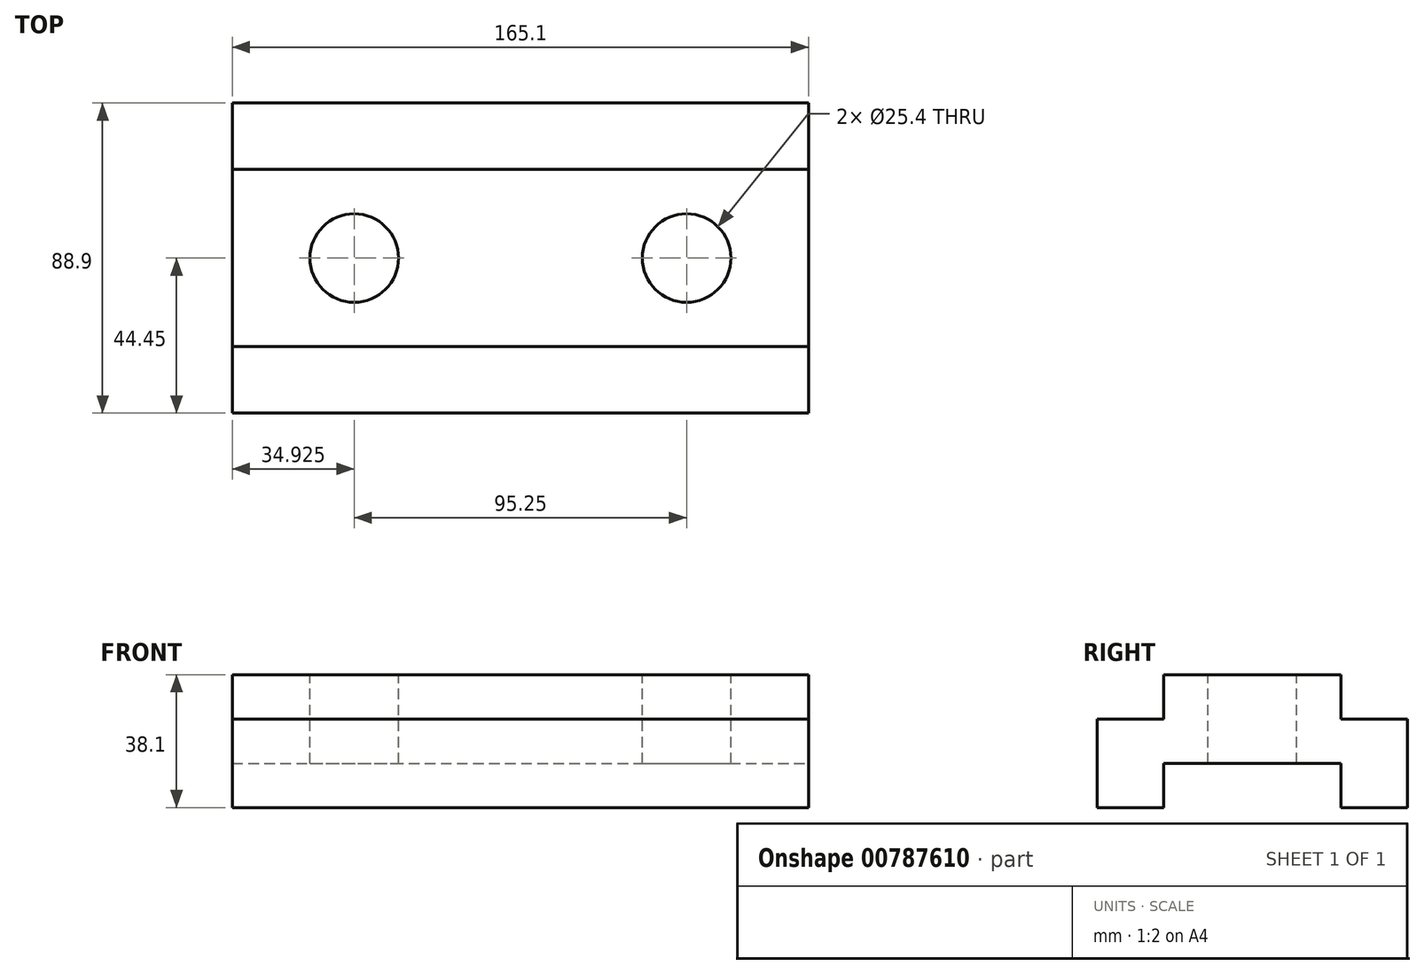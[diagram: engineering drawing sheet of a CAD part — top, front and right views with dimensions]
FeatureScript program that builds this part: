
annotation { "Feature Type Name" : "Feature", "Feature Type Description" : "" }
export const myFeature = defineFeature(function(context is Context, id is Id, definition is map)
    precondition{}
    {
        {
            var Q0;
            Q0=qCreatedBy(makeId("Right.planeOp"),FACE);
            var sketch = newSketch(context, id + "F0", { "sketchPlane" : qUnion([Q0])});
            skLineSegment(sketch, "E0", {"start": v(0, 0) * mm, "end": v(0, 25.4) * mm});
            skLineSegment(sketch, "E1", {"start": v(0, 25.4) * mm, "end": v(19.05, 25.4) * mm});
            skLineSegment(sketch, "E2", {"start": v(19.05, 25.4) * mm, "end": v(19.05, 38.1) * mm});
            skLineSegment(sketch, "E3", {"start": v(19.05, 38.1) * mm, "end": v(69.85, 38.1) * mm});
            skLineSegment(sketch, "E4", {"start": v(69.85, 38.1) * mm, "end": v(69.85, 25.4) * mm});
            skLineSegment(sketch, "E5", {"start": v(69.85, 25.4) * mm, "end": v(88.9, 25.4) * mm});
            skLineSegment(sketch, "E6", {"start": v(88.9, 25.4) * mm, "end": v(88.9, 0) * mm});
            skLineSegment(sketch, "E7", {"start": v(88.9, 0) * mm, "end": v(0, 0) * mm});
            skSolve(sketch);
        }
        {
            var Q0;
            Q0=makeQuery(id+"F0.imprint","IMPRINT",FACE,{"disambiguationData":[TD([[makeQuery(id+"F0.imprint","IMPRINT",EDGE,{"derivedFrom":sQuery(id+"F0.wireOp",EDGE,"E0")}),-1.0]])]});
            extrude(context, id + "F1", {"entities" : qUnion([Q0]), "depth" : 165.1 * mm, "offsetDistance" : 25.4 * mm});
        }
        {
            var Q0;
            Q0=makeQuery(id+"F1.opExtrude","CAP_FACE",FACE,{"disambiguationData":[OSD([sQuery(id+"F0.wireOp",EDGE,"E0"),sQuery(id+"F0.wireOp",EDGE,"E1"),sQuery(id+"F0.wireOp",EDGE,"E2"),sQuery(id+"F0.wireOp",EDGE,"E3"),sQuery(id+"F0.wireOp",EDGE,"E4"),sQuery(id+"F0.wireOp",EDGE,"E5"),sQuery(id+"F0.wireOp",EDGE,"E6"),sQuery(id+"F0.wireOp",EDGE,"E7")])],"isStart":false});
            var sketch = newSketch(context, id + "F2", { "sketchPlane" : qUnion([Q0])});
            skLineSegment(sketch, "E8", {"start": v(0, 0) * mm, "end": v(19.05, 0) * mm});
            skLineSegment(sketch, "E9", {"start": v(19.05, 0) * mm, "end": v(19.05, 12.7) * mm});
            skLineSegment(sketch, "E10", {"start": v(19.05, 12.7) * mm, "end": v(69.85, 12.7) * mm});
            skLineSegment(sketch, "E11", {"start": v(69.85, 12.7) * mm, "end": v(69.85, 0) * mm});
            skLineSegment(sketch, "E12", {"start": v(69.85, 0) * mm, "end": v(88.9, 0) * mm});
            skSolve(sketch);
        }
        {
            var Q0;
            {var subQ0=sQuery(id+"F2.wireOp",EDGE,"E9");Q0=makeQuery(id+"F2.imprint","IMPRINT",FACE,{"disambiguationData":[TD([[makeQuery(id+"F2.imprint","IMPRINT",EDGE,{"derivedFrom":subQ0}),-1.0]])]});}
            extrude(context, id + "F3", {"entities" : qUnion([Q0]), "operationType" : NewBodyOperationType.REMOVE, "endBound" : BoundingType.THROUGH_ALL, "oppositeDirection" : true, "depth" : 25.4 * mm, "offsetDistance" : 25.4 * mm});
        }
        {
            var Q0;
            Q0=makeQuery(id+"F1.opExtrude","SWEPT_FACE",FACE,{"disambiguationData":[OSD([sQuery(id+"F0.wireOp",EDGE,"E3")])]});
            var sketch = newSketch(context, id + "F4", { "sketchPlane" : qUnion([Q0])});
            skLineSegment(sketch, "E13", {"start": v(0, 44.45) * mm, "end": v(34.92, 44.45) * mm, "construction": true});
            skLineSegment(sketch, "E14", {"start": v(34.92, 44.45) * mm, "end": v(130.18, 44.45) * mm, "construction": true});
            skCircle(sketch, "E15", {"center": v(34.92, 44.45) * mm, "radius": 12.7 * mm});
            skCircle(sketch, "E16", {"center": v(130.18, 44.45) * mm, "radius": 12.7 * mm});
            skSolve(sketch);
        }
        {
            var Q0;
            Q0=makeQuery(id+"F4.imprint","IMPRINT",FACE,{"disambiguationData":[TD([[makeQuery(id+"F4.imprint","IMPRINT",EDGE,{"derivedFrom":sQuery(id+"F4.wireOp",EDGE,"E15")}),1.0]])]});
            var Q1;
            Q1=makeQuery(id+"F4.imprint","IMPRINT",FACE,{"disambiguationData":[TD([[makeQuery(id+"F4.imprint","IMPRINT",EDGE,{"derivedFrom":sQuery(id+"F4.wireOp",EDGE,"E16")}),1.0]])]});
            extrude(context, id + "F5", {"entities" : qUnion([Q0, Q1]), "operationType" : NewBodyOperationType.REMOVE, "endBound" : BoundingType.THROUGH_ALL, "oppositeDirection" : true, "depth" : 25.4 * mm, "offsetDistance" : 25.4 * mm});
        }
    });
